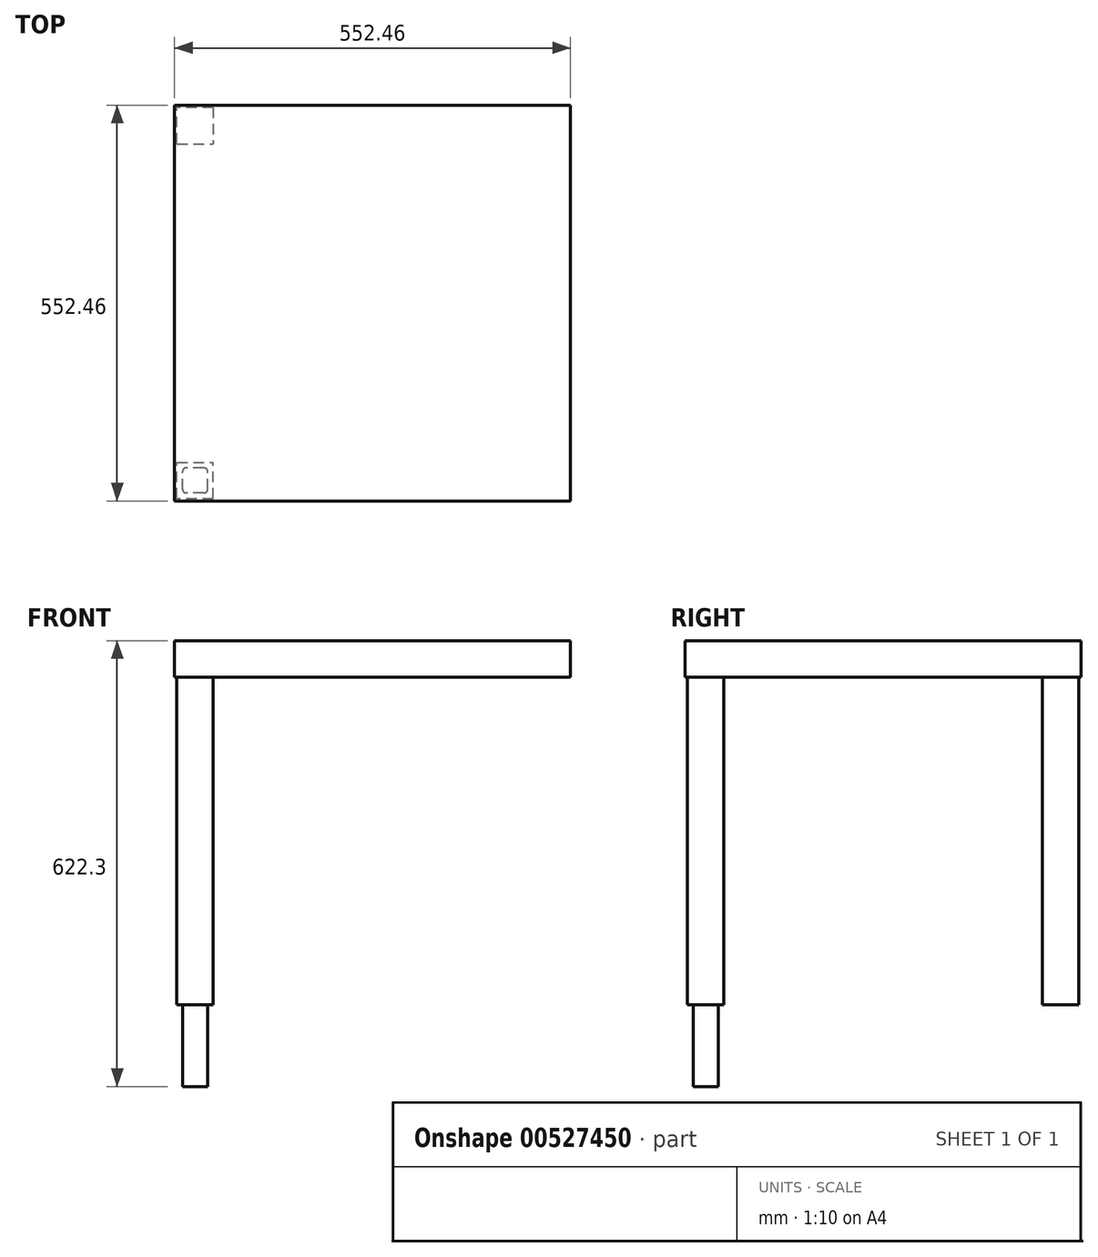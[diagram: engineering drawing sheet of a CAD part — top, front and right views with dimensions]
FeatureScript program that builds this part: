
annotation { "Feature Type Name" : "Feature", "Feature Type Description" : "" }
export const myFeature = defineFeature(function(context is Context, id is Id, definition is map)
    precondition{}
    {
        {
            var Q0;
            Q0=qCreatedBy(makeId("Top.planeOp"),FACE);
            var sketch = newSketch(context, id + "F0", { "sketchPlane" : qUnion([Q0])});
            skLineSegment(sketch, "E0.bottom", {"start": v(273.05, 273.05) * mm, "end": v(-273.05, 273.05) * mm});
            skLineSegment(sketch, "E0.top", {"start": v(273.05, -273.05) * mm, "end": v(-273.05, -273.05) * mm});
            skLineSegment(sketch, "E0.left", {"start": v(273.05, 273.05) * mm, "end": v(273.05, -273.05) * mm});
            skLineSegment(sketch, "E0.right", {"start": v(-273.05, 273.05) * mm, "end": v(-273.05, -273.05) * mm});
            skPoint(sketch, "E0.middle", {"position": v(0, 0) * mm});
            skSolve(sketch);
        }
        {
            var Q0;
            Q0=qCreatedBy(makeId("Top.planeOp"),FACE);
            var sketch = newSketch(context, id + "F1", { "sketchPlane" : qUnion([Q0])});
            skLineSegment(sketch, "E1.bottom", {"start": v(-273.05, 273.05) * mm, "end": v(-222.25, 273.05) * mm});
            skLineSegment(sketch, "E1.top", {"start": v(-273.05, 222.25) * mm, "end": v(-222.25, 222.25) * mm});
            skLineSegment(sketch, "E1.left", {"start": v(-273.05, 273.05) * mm, "end": v(-273.05, 222.25) * mm});
            skLineSegment(sketch, "E1.right", {"start": v(-222.25, 273.05) * mm, "end": v(-222.25, 222.25) * mm});
            skPoint(sketch, "E2.0", {"position": v(-273.05, 273.05) * mm});
            skSolve(sketch);
        }
        {
            var Q0;
            Q0=makeQuery(id+"F1.imprint","IMPRINT",FACE,{"disambiguationData":[TD([[makeQuery(id+"F1.imprint","IMPRINT",EDGE,{"derivedFrom":sQuery(id+"F1.wireOp",EDGE,"E1.bottom")}),-1.0]])]});
            extrude(context, id + "F2", {"entities" : qUnion([Q0]), "depth" : 508 * mm, "offsetDistance" : 25.4 * mm});
        }
        {
            var Q0;
            Q0=makeQuery(id+"F2.opExtrude","SWEPT_BODY",BODY,{"disambiguationData":[OSD([sQuery(id+"F1.wireOp",EDGE,"E1.bottom"),sQuery(id+"F1.wireOp",EDGE,"E1.top"),sQuery(id+"F1.wireOp",EDGE,"E1.left"),sQuery(id+"F1.wireOp",EDGE,"E1.right")])]});
            var Q1;
            Q1=qCreatedBy(makeId("Right.planeOp"),FACE);
            mirror(context, id + "F3", {"entities" : qUnion([Q0]), "mirrorPlane" : qUnion([Q1])});
        }
        {
            var Q0;
            Q0=makeQuery(id+"F2.opExtrude","SWEPT_BODY",BODY,{"disambiguationData":[OSD([sQuery(id+"F1.wireOp",EDGE,"E1.bottom"),sQuery(id+"F1.wireOp",EDGE,"E1.top"),sQuery(id+"F1.wireOp",EDGE,"E1.left"),sQuery(id+"F1.wireOp",EDGE,"E1.right")])]});
            var Q1;
            Q1=makeQuery(id+"F3.opPattern","COPY",BODY,{"derivedFrom":makeQuery(id+"F2.opExtrude","SWEPT_BODY",BODY,{"disambiguationData":[OSD([sQuery(id+"F1.wireOp",EDGE,"E1.bottom"),sQuery(id+"F1.wireOp",EDGE,"E1.top"),sQuery(id+"F1.wireOp",EDGE,"E1.left"),sQuery(id+"F1.wireOp",EDGE,"E1.right")])]}),"instanceName":"1"});
            var Q2;
            Q2=qCreatedBy(makeId("Front.planeOp"),FACE);
            mirror(context, id + "F4", {"entities" : qUnion([Q0, Q1]), "mirrorPlane" : qUnion([Q2])});
        }
        {
            var Q0;
            Q0=makeQuery(id+"F2.opExtrude","CAP_FACE",FACE,{"disambiguationData":[OSD([sQuery(id+"F1.wireOp",EDGE,"E1.bottom"),sQuery(id+"F1.wireOp",EDGE,"E1.top"),sQuery(id+"F1.wireOp",EDGE,"E1.left"),sQuery(id+"F1.wireOp",EDGE,"E1.right")])],"isStart":false});
            var sketch = newSketch(context, id + "F5", { "sketchPlane" : qUnion([Q0])});
            skLineSegment(sketch, "E3.0.0", {"start": v(-273.05, -273.05) * mm, "end": v(273.05, -273.05) * mm});
            skLineSegment(sketch, "E3.0.1", {"start": v(273.05, -273.05) * mm, "end": v(273.05, 273.05) * mm});
            skLineSegment(sketch, "E3.0.2", {"start": v(273.05, 273.05) * mm, "end": v(-273.05, 273.05) * mm});
            skLineSegment(sketch, "E3.0.3", {"start": v(-273.05, 273.05) * mm, "end": v(-273.05, -273.05) * mm});
            skSolve(sketch);
        }
        {
            var Q0;
            {var subQ2=sQuery(id+"F5.wireOp",EDGE,"E3.0.0");Q0=makeQuery(id+"F5.imprint","IMPRINT",FACE,{"disambiguationData":[TD([[makeQuery(id+"F5.imprint","IMPRINT",EDGE,{"derivedFrom":subQ2}),1.0]])]});}
            var Q1;
            {var subQ4=makeQuery(id+"F2.opExtrude","CAP_EDGE",EDGE,{"disambiguationData":[OSD([sQuery(id+"F1.wireOp",EDGE,"E1.top")])],"isStart":false});Q1=makeQuery(id+"F5.imprint","IMPRINT",FACE,{"disambiguationData":[TD([[makeQuery(id+"F5.imprint","IMPRINT",EDGE,{"derivedFrom":subQ4}),1.0]])]});}
            extrude(context, id + "F6", {"entities" : qUnion([Q0, Q1]), "oppositeDirection" : true, "depth" : 50.8 * mm, "offsetDistance" : 25.4 * mm});
        }
        {
            var Q0;
            Q0=makeQuery(id+"F2.opExtrude","SWEPT_BODY",BODY,{"disambiguationData":[OSD([sQuery(id+"F1.wireOp",EDGE,"E1.bottom"),sQuery(id+"F1.wireOp",EDGE,"E1.top"),sQuery(id+"F1.wireOp",EDGE,"E1.left"),sQuery(id+"F1.wireOp",EDGE,"E1.right")])]});
            var Q1;
            Q1=makeQuery(id+"F6.opExtrude","SWEPT_BODY",BODY,{"disambiguationData":[OSD([sQuery(id+"F5.wireOp",EDGE,"E3.0.0"),sQuery(id+"F5.wireOp",EDGE,"E3.0.1"),sQuery(id+"F5.wireOp",EDGE,"E3.0.2"),sQuery(id+"F5.wireOp",EDGE,"E3.0.3")])]});
            var Q2;
            Q2=makeQuery(id+"F3.opPattern","COPY",BODY,{"derivedFrom":makeQuery(id+"F2.opExtrude","SWEPT_BODY",BODY,{"disambiguationData":[OSD([sQuery(id+"F1.wireOp",EDGE,"E1.bottom"),sQuery(id+"F1.wireOp",EDGE,"E1.top"),sQuery(id+"F1.wireOp",EDGE,"E1.left"),sQuery(id+"F1.wireOp",EDGE,"E1.right")])]}),"instanceName":"1"});
            var Q3;
            Q3=makeQuery(id+"F4.opPattern","COPY",BODY,{"derivedFrom":makeQuery(id+"F2.opExtrude","SWEPT_BODY",BODY,{"disambiguationData":[OSD([sQuery(id+"F1.wireOp",EDGE,"E1.bottom"),sQuery(id+"F1.wireOp",EDGE,"E1.top"),sQuery(id+"F1.wireOp",EDGE,"E1.left"),sQuery(id+"F1.wireOp",EDGE,"E1.right")])]}),"instanceName":"1"});
            var Q4;
            Q4=makeQuery(id+"F4.opPattern","COPY",BODY,{"derivedFrom":makeQuery(id+"F3.opPattern","COPY",BODY,{"derivedFrom":makeQuery(id+"F2.opExtrude","SWEPT_BODY",BODY,{"disambiguationData":[OSD([sQuery(id+"F1.wireOp",EDGE,"E1.bottom"),sQuery(id+"F1.wireOp",EDGE,"E1.top"),sQuery(id+"F1.wireOp",EDGE,"E1.left"),sQuery(id+"F1.wireOp",EDGE,"E1.right")])]}),"instanceName":"1"}),"instanceName":"1"});
            booleanBodies(context, id + "F7", {"operationType" : BooleanOperationType.UNION, "tools" : qUnion([Q0, Q1, Q2, Q3, Q4])});
        }
        {
            var Q0;
            Q0=makeQuery(id+"F7.opBoolean","MERGE",FACE,{"derivedFrom":[makeQuery(id+"F2.opExtrude","CAP_FACE",FACE,{"disambiguationData":[OSD([sQuery(id+"F1.wireOp",EDGE,"E1.bottom"),sQuery(id+"F1.wireOp",EDGE,"E1.top"),sQuery(id+"F1.wireOp",EDGE,"E1.left"),sQuery(id+"F1.wireOp",EDGE,"E1.right")])],"isStart":false}),makeQuery(id+"F6.opExtrude","CAP_FACE",FACE,{"disambiguationData":[OSD([sQuery(id+"F5.wireOp",EDGE,"E3.0.0"),sQuery(id+"F5.wireOp",EDGE,"E3.0.1"),sQuery(id+"F5.wireOp",EDGE,"E3.0.2"),sQuery(id+"F5.wireOp",EDGE,"E3.0.3")])],"isStart":true})]});
            var sketch = newSketch(context, id + "F8", { "sketchPlane" : qUnion([Q0])});
            skLineSegment(sketch, "E4.0", {"start": v(-276.23, 276.23) * mm, "end": v(-276.23, -276.22) * mm});
            skLineSegment(sketch, "E4.1", {"start": v(276.22, 276.23) * mm, "end": v(-276.23, 276.23) * mm});
            skLineSegment(sketch, "E4.2", {"start": v(276.23, -276.23) * mm, "end": v(276.22, 276.22) * mm});
            skLineSegment(sketch, "E4.3", {"start": v(-276.23, -276.23) * mm, "end": v(276.23, -276.23) * mm});
            skSolve(sketch);
        }
        {
            var Q0;
            Q0=makeQuery(id+"F8.imprint","IMPRINT",FACE,{"disambiguationData":[TD([[makeQuery(id+"F8.imprint","IMPRINT",EDGE,{"derivedFrom":sQuery(id+"F8.wireOp",EDGE,"E4.0")}),1.0]])]});
            var Q1;
            Q1=makeQuery(id+"F6.opExtrude","CAP_FACE",FACE,{"disambiguationData":[OSD([sQuery(id+"F5.wireOp",EDGE,"E3.0.0"),sQuery(id+"F5.wireOp",EDGE,"E3.0.1"),sQuery(id+"F5.wireOp",EDGE,"E3.0.2"),sQuery(id+"F5.wireOp",EDGE,"E3.0.3")])],"isStart":false});
            extrude(context, id + "F9", {"entities" : qUnion([Q0]), "operationType" : NewBodyOperationType.ADD, "endBound" : BoundingType.UP_TO_SURFACE, "oppositeDirection" : true, "depth" : 25.4 * mm, "endBoundEntityFace" : qUnion([Q1]), "offsetDistance" : 25.4 * mm});
        }
        {
            var Q0;
            Q0=makeQuery(id+"F4.opPattern","COPY",FACE,{"derivedFrom":makeQuery(id+"F3.opPattern","COPY",FACE,{"derivedFrom":makeQuery(id+"F2.opExtrude","CAP_FACE",FACE,{"disambiguationData":[OSD([sQuery(id+"F1.wireOp",EDGE,"E1.bottom"),sQuery(id+"F1.wireOp",EDGE,"E1.top"),sQuery(id+"F1.wireOp",EDGE,"E1.left"),sQuery(id+"F1.wireOp",EDGE,"E1.right")])],"isStart":true}),"instanceName":"1"}),"instanceName":"1"});
            var Q1;
            Q1=makeQuery(id+"F3.opPattern","COPY",FACE,{"derivedFrom":makeQuery(id+"F2.opExtrude","CAP_FACE",FACE,{"disambiguationData":[OSD([sQuery(id+"F1.wireOp",EDGE,"E1.bottom"),sQuery(id+"F1.wireOp",EDGE,"E1.top"),sQuery(id+"F1.wireOp",EDGE,"E1.left"),sQuery(id+"F1.wireOp",EDGE,"E1.right")])],"isStart":true}),"instanceName":"1"});
            var Q2;
            {var subQ0=sQuery(id+"F5.wireOp",EDGE,"E3.0.3");var subQ1=sQuery(id+"F5.wireOp",EDGE,"E3.0.2");var subQ2=sQuery(id+"F5.wireOp",EDGE,"E3.0.1");var subQ3=sQuery(id+"F5.wireOp",EDGE,"E3.0.0");Q2=makeQuery(id+"F9.boolean.opBoolean","MERGE",FACE,{"derivedFrom":[makeQuery(id+"F6.opExtrude","CAP_FACE",FACE,{"disambiguationData":[OSD([subQ3,subQ2,subQ1,subQ0])],"isStart":false}),makeQuery(id+"F9.opExtrude","CAP_FACE",FACE,{"disambiguationData":[OSD([subQ3,subQ2,subQ1,subQ0])],"isStart":false})]});}
            extrude(context, id + "F10", {"entities" : qUnion([Q0, Q1]), "operationType" : NewBodyOperationType.REMOVE, "endBound" : BoundingType.UP_TO_SURFACE, "oppositeDirection" : true, "depth" : 25.4 * mm, "endBoundEntityFace" : qUnion([Q2]), "offsetDistance" : 25.4 * mm});
        }
        {
            var Q0;
            Q0=makeQuery(id+"F4.opPattern","COPY",FACE,{"derivedFrom":makeQuery(id+"F2.opExtrude","CAP_FACE",FACE,{"disambiguationData":[OSD([sQuery(id+"F1.wireOp",EDGE,"E1.bottom"),sQuery(id+"F1.wireOp",EDGE,"E1.top"),sQuery(id+"F1.wireOp",EDGE,"E1.left"),sQuery(id+"F1.wireOp",EDGE,"E1.right")])],"isStart":true}),"instanceName":"1"});
            var sketch = newSketch(context, id + "F11", { "sketchPlane" : qUnion([Q0])});
            skLineSegment(sketch, "E5", {"start": v(-273.05, 273.05) * mm, "end": v(-222.25, 222.25) * mm});
            skLineSegment(sketch, "E6.bottom", {"start": v(-230.12, 265.18) * mm, "end": v(-265.18, 265.18) * mm});
            skLineSegment(sketch, "E6.top", {"start": v(-230.12, 230.12) * mm, "end": v(-265.18, 230.12) * mm});
            skLineSegment(sketch, "E6.left", {"start": v(-230.12, 265.18) * mm, "end": v(-230.12, 230.12) * mm});
            skLineSegment(sketch, "E6.right", {"start": v(-265.18, 265.18) * mm, "end": v(-265.18, 230.12) * mm});
            skPoint(sketch, "E6.middle", {"position": v(-247.65, 247.65) * mm});
            skSolve(sketch);
        }
        {
            var Q0;
            {var subQ0=sQuery(id+"F11.wireOp",EDGE,"E6.bottom");Q0=makeQuery(id+"F11.imprint","IMPRINT",FACE,{"disambiguationData":[TD([[makeQuery(id+"F11.imprint","IMPRINT",EDGE,{"derivedFrom":subQ0}),1.0]])]});}
            var Q1;
            {var subQ2=sQuery(id+"F11.wireOp",EDGE,"E6.top");Q1=makeQuery(id+"F11.imprint","IMPRINT",FACE,{"disambiguationData":[TD([[makeQuery(id+"F11.imprint","IMPRINT",EDGE,{"derivedFrom":subQ2}),-1.0]])]});}
            extrude(context, id + "F12", {"entities" : qUnion([Q0, Q1]), "operationType" : NewBodyOperationType.ADD, "depth" : 114.3 * mm, "offsetDistance" : 25.4 * mm});
        }
        {
            var Q0;
            Q0=makeQuery(id+"F12.opExtrude","SWEPT_EDGE",EDGE,{"disambiguationData":[OSD([sQuery(id+"F11.wireOp",EDGE,"E6.bottom"),sQuery(id+"F11.wireOp",EDGE,"E6.left")])]});
            var Q1;
            Q1=makeQuery(id+"F12.opExtrude","SWEPT_EDGE",EDGE,{"disambiguationData":[OSD([sQuery(id+"F11.wireOp",EDGE,"E5"),sQuery(id+"F11.wireOp",EDGE,"E6.bottom"),sQuery(id+"F11.wireOp",EDGE,"E6.right")])]});
            var Q2;
            Q2=makeQuery(id+"F12.opExtrude","SWEPT_EDGE",EDGE,{"disambiguationData":[OSD([sQuery(id+"F11.wireOp",EDGE,"E5"),sQuery(id+"F11.wireOp",EDGE,"E6.top"),sQuery(id+"F11.wireOp",EDGE,"E6.left")])]});
            var Q3;
            Q3=makeQuery(id+"F12.opExtrude","SWEPT_EDGE",EDGE,{"disambiguationData":[OSD([sQuery(id+"F11.wireOp",EDGE,"E6.top"),sQuery(id+"F11.wireOp",EDGE,"E6.right")])]});
            fillet(context, id + "F13", {"entities" : qUnion([Q0, Q1, Q2, Q3]), "radius" : 5.08 * mm, "tangentPropagation" : true, "allowEdgeOverflow" : false});
        }
    });
